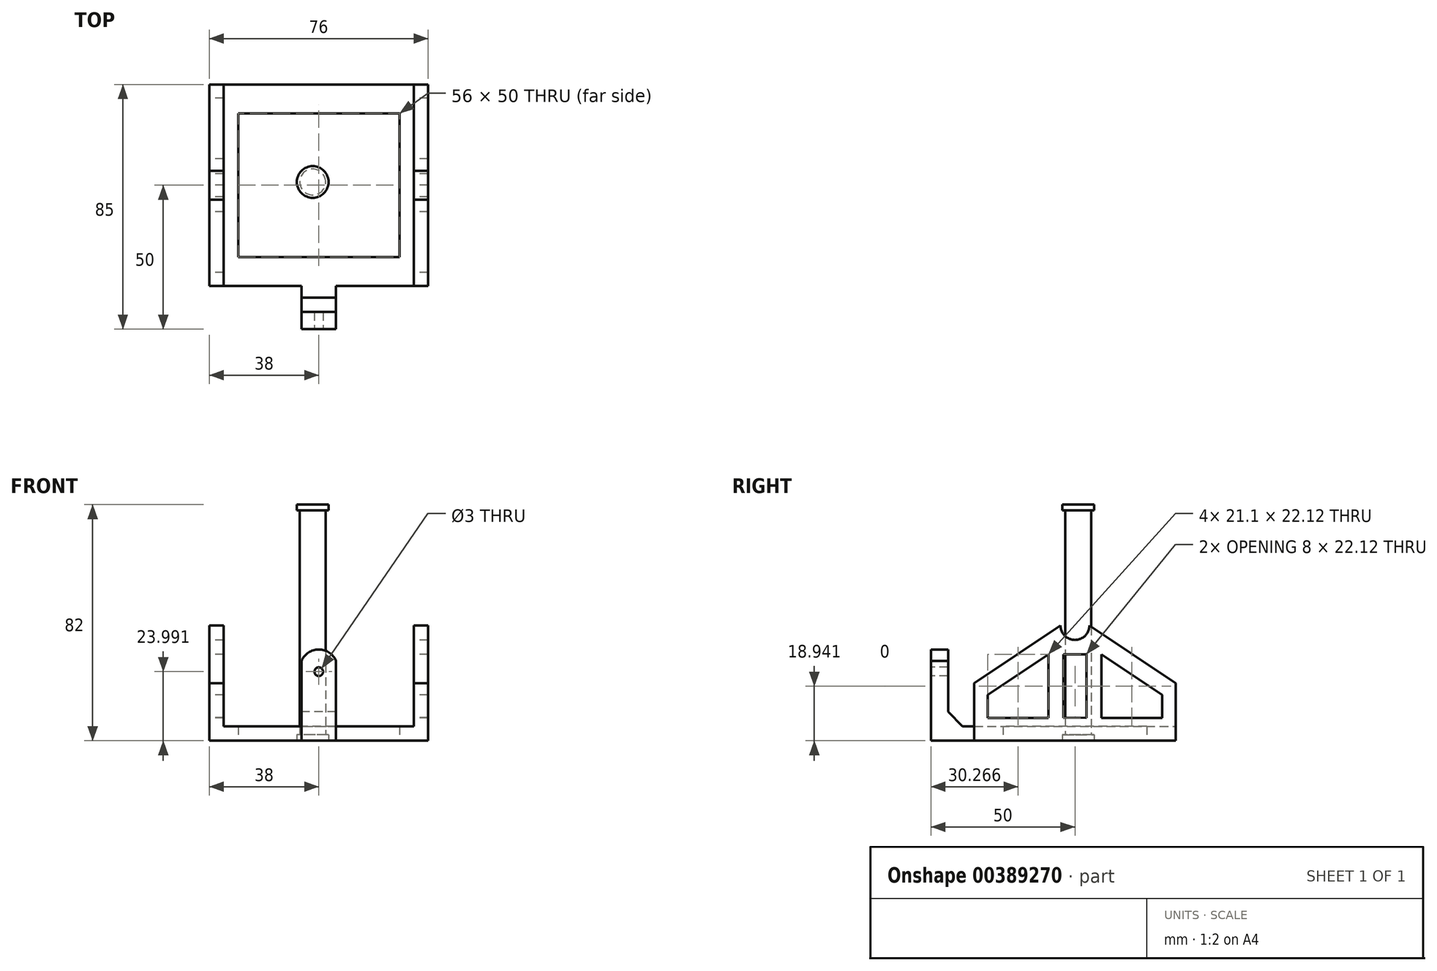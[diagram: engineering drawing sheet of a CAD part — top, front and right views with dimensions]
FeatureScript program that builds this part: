
annotation { "Feature Type Name" : "Feature", "Feature Type Description" : "" }
export const myFeature = defineFeature(function(context is Context, id is Id, definition is map)
    precondition{}
    {
        {
            var Q0;
            Q0=qCreatedBy(makeId("Top.planeOp"),FACE);
            var sketch = newSketch(context, id + "F0", { "sketchPlane" : qUnion([Q0])});
            skLineSegment(sketch, "E0.bottom", {"start": v(0, 0) * mm, "end": v(-76, 0) * mm});
            skLineSegment(sketch, "E0.top", {"start": v(0, 70) * mm, "end": v(-76, 70) * mm});
            skLineSegment(sketch, "E0.left", {"start": v(0, 0) * mm, "end": v(0, 70) * mm});
            skLineSegment(sketch, "E0.right", {"start": v(-76, 0) * mm, "end": v(-76, 70) * mm});
            skLineSegment(sketch, "E1", {"start": v(-38, 70) * mm, "end": v(-38, 0) * mm, "construction": true});
            skLineSegment(sketch, "E2.bottom", {"start": v(-38, -15) * mm, "end": v(-44, -15) * mm});
            skLineSegment(sketch, "E2.top", {"start": v(-38, 0) * mm, "end": v(-44, 0) * mm});
            skLineSegment(sketch, "E2.right", {"start": v(-44, -15) * mm, "end": v(-44, 0) * mm});
            skLineSegment(sketch, "E3.bottom", {"start": v(-38, -15) * mm, "end": v(-32, -15) * mm});
            skLineSegment(sketch, "E3.top", {"start": v(-38, 0) * mm, "end": v(-32, 0) * mm});
            skLineSegment(sketch, "E3.right", {"start": v(-32, -15) * mm, "end": v(-32, 0) * mm});
            skLineSegment(sketch, "E4.trimOffspring", {"start": v(-38, -15) * mm, "end": v(-38, -41) * mm, "construction": true});
            skLineSegment(sketch, "E5", {"start": v(-38, 0) * mm, "end": v(-38, -17.1) * mm, "construction": true});
            skLineSegment(sketch, "E6", {"start": v(-44, -9) * mm, "end": v(-32, -9) * mm});
            skLineSegment(sketch, "E7.bottom", {"start": v(-66, 60) * mm, "end": v(-10, 60) * mm});
            skLineSegment(sketch, "E7.top", {"start": v(-66, 10) * mm, "end": v(-10, 10) * mm});
            skLineSegment(sketch, "E7.left", {"start": v(-66, 60) * mm, "end": v(-66, 10) * mm});
            skLineSegment(sketch, "E7.right", {"start": v(-10, 60) * mm, "end": v(-10, 10) * mm});
            skLineSegment(sketch, "E8", {"start": v(-66, 10) * mm, "end": v(-66, 0) * mm});
            skLineSegment(sketch, "E9", {"start": v(-66, 60) * mm, "end": v(-66, 70) * mm});
            skLineSegment(sketch, "E10", {"start": v(-10, 60) * mm, "end": v(-10, 70) * mm});
            skLineSegment(sketch, "E11", {"start": v(-10, 10) * mm, "end": v(-10, 0) * mm});
            skLineSegment(sketch, "E12", {"start": v(-71, 70) * mm, "end": v(-71, 0) * mm});
            skLineSegment(sketch, "E13", {"start": v(-5, 70) * mm, "end": v(-5, 0) * mm});
            skSolve(sketch);
        }
        {
            var Q0;
            Q0 = qSketchRegion(id + "F0", true);
            extrude(context, id + "F1", {"entities" : qUnion([Q0]), "depth" : 5 * mm, "offsetDistance" : 25 * mm});
        }
        {
            var Q0;
            {var subQ2=sQuery(id+"F0.wireOp",EDGE,"E2.bottom");Q0=makeQuery(id+"F0.imprint","IMPRINT",FACE,{"disambiguationData":[TD([[makeQuery(id+"F0.imprint","IMPRINT",EDGE,{"derivedFrom":subQ2}),-1.0]])]});}
            extrude(context, id + "F2", {"entities" : qUnion([Q0]), "operationType" : NewBodyOperationType.ADD, "depth" : 35 * mm, "offsetDistance" : 25 * mm});
        }
        {
            var Q0;
            {var subQ0=sQuery(id+"F0.wireOp",EDGE,"E0.right");Q0=makeQuery(id+"F0.imprint","IMPRINT",FACE,{"disambiguationData":[TD([[makeQuery(id+"F0.imprint","IMPRINT",EDGE,{"derivedFrom":subQ0}),-1.0]])]});}
            var Q1;
            {var subQ0=sQuery(id+"F0.wireOp",EDGE,"E0.left");Q1=makeQuery(id+"F0.imprint","IMPRINT",FACE,{"disambiguationData":[TD([[makeQuery(id+"F0.imprint","IMPRINT",EDGE,{"derivedFrom":subQ0}),1.0]])]});}
            extrude(context, id + "F3", {"entities" : qUnion([Q0, Q1]), "operationType" : NewBodyOperationType.ADD, "depth" : 45 * mm, "offsetDistance" : 25 * mm});
        }
        {
            var Q0;
            {var subQ0=sQuery(id+"F0.wireOp",EDGE,"E0.right");Q0=makeQuery(id+"F3.boolean.opBoolean","MERGE",FACE,{"derivedFrom":[makeQuery(id+"F1.opExtrude","SWEPT_FACE",FACE,{"disambiguationData":[OSD([subQ0])]}),makeQuery(id+"F3.opExtrude","SWEPT_FACE",FACE,{"disambiguationData":[OSD([subQ0])]})]});}
            var sketch = newSketch(context, id + "F4", { "sketchPlane" : qUnion([Q0])});
            skLineSegment(sketch, "E14", {"start": v(-70, 5) * mm, "end": v(0, 5) * mm, "construction": true});
            skCircle(sketch, "E15", {"center": v(-35, 40) * mm, "radius": 5 * mm});
            skCircle(sketch, "E16", {"center": v(-35, 40) * mm, "radius": 32 * mm, "construction": true});
            skLineSegment(sketch, "E17", {"start": v(-35, 5) * mm, "end": v(-35, 67.3) * mm, "construction": true});
            skLineSegment(sketch, "E18", {"start": v(-40, 40.08) * mm, "end": v(-70, 40.08) * mm, "construction": true});
            skLineSegment(sketch, "E19", {"start": v(-70, 40.08) * mm, "end": v(0, 40.08) * mm, "construction": true});
            skLineSegment(sketch, "E20", {"start": v(-40, 40.08) * mm, "end": v(-70, 20) * mm});
            skLineSegment(sketch, "E21", {"start": v(-30, 40.08) * mm, "end": v(0, 20) * mm});
            skLineSegment(sketch, "E22.left", {"start": v(-39, 30) * mm, "end": v(-39, 7.88) * mm});
            skLineSegment(sketch, "E23", {"start": v(-44.19, 30) * mm, "end": v(-44.19, 7.88) * mm});
            skLineSegment(sketch, "E24", {"start": v(-44.19, 7.88) * mm, "end": v(-65.28, 7.88) * mm});
            skLineSegment(sketch, "E25", {"start": v(-65.28, 7.88) * mm, "end": v(-65.28, 15.88) * mm});
            skLineSegment(sketch, "E26", {"start": v(-65.28, 15.88) * mm, "end": v(-44.19, 30) * mm});
            skLineSegment(sketch, "E27", {"start": v(-35, 30) * mm, "end": v(-35, 8) * mm});
            skLineSegment(sketch, "E28", {"start": v(-39, 30) * mm, "end": v(-35, 30) * mm});
            skLineSegment(sketch, "E29", {"start": v(-35, 8) * mm, "end": v(-39, 7.88) * mm});
            skLineSegment(sketch, "E30.MirrorCS", {"start": v(-31, 30) * mm, "end": v(-35, 30) * mm});
            skLineSegment(sketch, "E31.MirrorCS", {"start": v(-31, 30) * mm, "end": v(-31, 7.88) * mm});
            skLineSegment(sketch, "E32.MirrorCS", {"start": v(-35, 8) * mm, "end": v(-31, 7.88) * mm});
            skLineSegment(sketch, "E33.MirrorCS", {"start": v(-25.81, 30) * mm, "end": v(-25.81, 7.88) * mm});
            skLineSegment(sketch, "E34.MirrorCS", {"start": v(-4.72, 15.88) * mm, "end": v(-25.81, 30) * mm});
            skLineSegment(sketch, "E35.MirrorCS", {"start": v(-4.72, 7.88) * mm, "end": v(-4.72, 15.88) * mm});
            skLineSegment(sketch, "E36.MirrorCS", {"start": v(-25.81, 7.88) * mm, "end": v(-4.72, 7.88) * mm});
            skSolve(sketch);
        }
        {
            var Q0;
            Q0 = qSketchRegion(id + "F4", true);
            var Q1;
            {var subQ0=sQuery(id+"F4.wireOp",EDGE,"E21");Q1=makeQuery(id+"F4.imprint","IMPRINT",FACE,{"disambiguationData":[TD([[makeQuery(id+"F4.imprint","IMPRINT",EDGE,{"derivedFrom":subQ0}),1.0]])]});}
            var Q2;
            {var subQ0=sQuery(id+"F4.wireOp",EDGE,"E20");Q2=makeQuery(id+"F4.imprint","IMPRINT",FACE,{"disambiguationData":[TD([[makeQuery(id+"F4.imprint","IMPRINT",EDGE,{"derivedFrom":subQ0}),-1.0]])]});}
            extrude(context, id + "F5", {"entities" : qUnion([Q0, Q1, Q2]), "operationType" : NewBodyOperationType.REMOVE, "endBound" : BoundingType.THROUGH_ALL, "oppositeDirection" : true, "depth" : 25 * mm, "offsetDistance" : 25 * mm});
        }
        {
            var Q0;
            {var subQ0=sQuery(id+"F0.wireOp",EDGE,"E3.bottom");var subQ1=sQuery(id+"F0.wireOp",EDGE,"E2.bottom");Q0=makeQuery(id+"F2.boolean.opBoolean","MERGE",FACE,{"derivedFrom":[makeQuery(id+"F1.opExtrude","SWEPT_FACE",FACE,{"disambiguationData":[OSD([subQ1,subQ0])]}),makeQuery(id+"F2.opExtrude","SWEPT_FACE",FACE,{"disambiguationData":[OSD([subQ1,subQ0])]})]});}
            var sketch = newSketch(context, id + "F6", { "sketchPlane" : qUnion([Q0])});
            skLineSegment(sketch, "E37", {"start": v(-38, 35) * mm, "end": v(-38, 0) * mm, "construction": true});
            skCircle(sketch, "E38", {"center": v(-38, 24) * mm, "radius": 1.5 * mm});
            skArc(sketch, "E39", {"start": v(-32, 27.73) * mm, "mid": v(-38.03, 31.7) * mm, "end": v(-44, 27.65) * mm});
            skSolve(sketch);
        }
        {
            var Q0;
            Q0=makeQuery(id+"F6.imprint","IMPRINT",FACE,{"disambiguationData":[TD([[makeQuery(id+"F6.imprint","IMPRINT",EDGE,{"derivedFrom":sQuery(id+"F6.wireOp",EDGE,"E38")}),1.0]])]});
            var Q1;
            {var subQ0=sQuery(id+"F6.wireOp",EDGE,"E39");Q1=makeQuery(id+"F6.imprint","IMPRINT",FACE,{"disambiguationData":[TD([[makeQuery(id+"F6.imprint","IMPRINT",EDGE,{"derivedFrom":subQ0}),-1.0]])]});}
            extrude(context, id + "F7", {"entities" : qUnion([Q0, Q1]), "operationType" : NewBodyOperationType.REMOVE, "endBound" : BoundingType.THROUGH_ALL, "oppositeDirection" : true, "depth" : 25 * mm, "offsetDistance" : 25 * mm});
        }
        {
            var Q0;
            Q0=makeQuery(id+"F2.boolean.opBoolean","INTERSECT",EDGE,{"derivedFrom":[makeQuery(id+"F1.opExtrude","CAP_FACE",FACE,{"disambiguationData":[OSD([sQuery(id+"F0.wireOp",EDGE,"E0.bottom"),sQuery(id+"F0.wireOp",EDGE,"E0.top"),sQuery(id+"F0.wireOp",EDGE,"E0.left"),sQuery(id+"F0.wireOp",EDGE,"E0.right"),sQuery(id+"F0.wireOp",EDGE,"E2.bottom"),sQuery(id+"F0.wireOp",EDGE,"E2.right"),sQuery(id+"F0.wireOp",EDGE,"E3.bottom"),sQuery(id+"F0.wireOp",EDGE,"E3.right"),sQuery(id+"F0.wireOp",EDGE,"E7.bottom"),sQuery(id+"F0.wireOp",EDGE,"E7.top"),sQuery(id+"F0.wireOp",EDGE,"E7.left"),sQuery(id+"F0.wireOp",EDGE,"E7.right")])],"isStart":false}),makeQuery(id+"F2.opExtrude","SWEPT_FACE",FACE,{"disambiguationData":[OSD([sQuery(id+"F0.wireOp",EDGE,"E6")])]})]});
            chamfer(context, id + "F8", {"entities" : qUnion([Q0]), "width" : 5 * mm, "tangentPropagation" : true});
        }
        {
            var Q0;
            Q0=qCreatedBy(makeId("Top.planeOp"),FACE);
            var sketch = newSketch(context, id + "F9", { "sketchPlane" : qUnion([Q0])});
            skCircle(sketch, "E40", {"center": v(-40.1, 36.13) * mm, "radius": 5.5 * mm});
            skSolve(sketch);
        }
        {
            var Q0;
            Q0 = qSketchRegion(id + "F9", true);
            extrude(context, id + "F10", {"entities" : qUnion([Q0]), "depth" : 2 * mm, "offsetDistance" : 25 * mm});
        }
        {
            var Q0;
            Q0=makeQuery(id+"F10.opExtrude","CAP_FACE",FACE,{"disambiguationData":[OSD([sQuery(id+"F9.wireOp",EDGE,"E40")])],"isStart":false});
            var sketch = newSketch(context, id + "F11", { "sketchPlane" : qUnion([Q0])});
            skCircle(sketch, "E41", {"center": v(-40.1, 36.13) * mm, "radius": 4.5 * mm});
            skSolve(sketch);
        }
        {
            var Q0;
            Q0=makeQuery(id+"F11.imprint","IMPRINT",FACE,{"disambiguationData":[TD([[makeQuery(id+"F11.imprint","IMPRINT",EDGE,{"derivedFrom":sQuery(id+"F11.wireOp",EDGE,"E41")}),1.0]])]});
            extrude(context, id + "F12", {"entities" : qUnion([Q0]), "operationType" : NewBodyOperationType.ADD, "depth" : 78 * mm, "offsetDistance" : 25 * mm});
        }
        {
            var Q0;
            Q0=makeQuery(id+"F12.opExtrude","CAP_FACE",FACE,{"disambiguationData":[OSD([sQuery(id+"F11.wireOp",EDGE,"E41")])],"isStart":false});
            var sketch = newSketch(context, id + "F13", { "sketchPlane" : qUnion([Q0])});
            skCircle(sketch, "E42", {"center": v(-40.1, 36.13) * mm, "radius": 5.5 * mm});
            skSolve(sketch);
        }
        {
            var Q0;
            Q0 = qSketchRegion(id + "F13", true);
            extrude(context, id + "F14", {"entities" : qUnion([Q0]), "operationType" : NewBodyOperationType.ADD, "depth" : 2 * mm, "offsetDistance" : 25 * mm});
        }
    });
